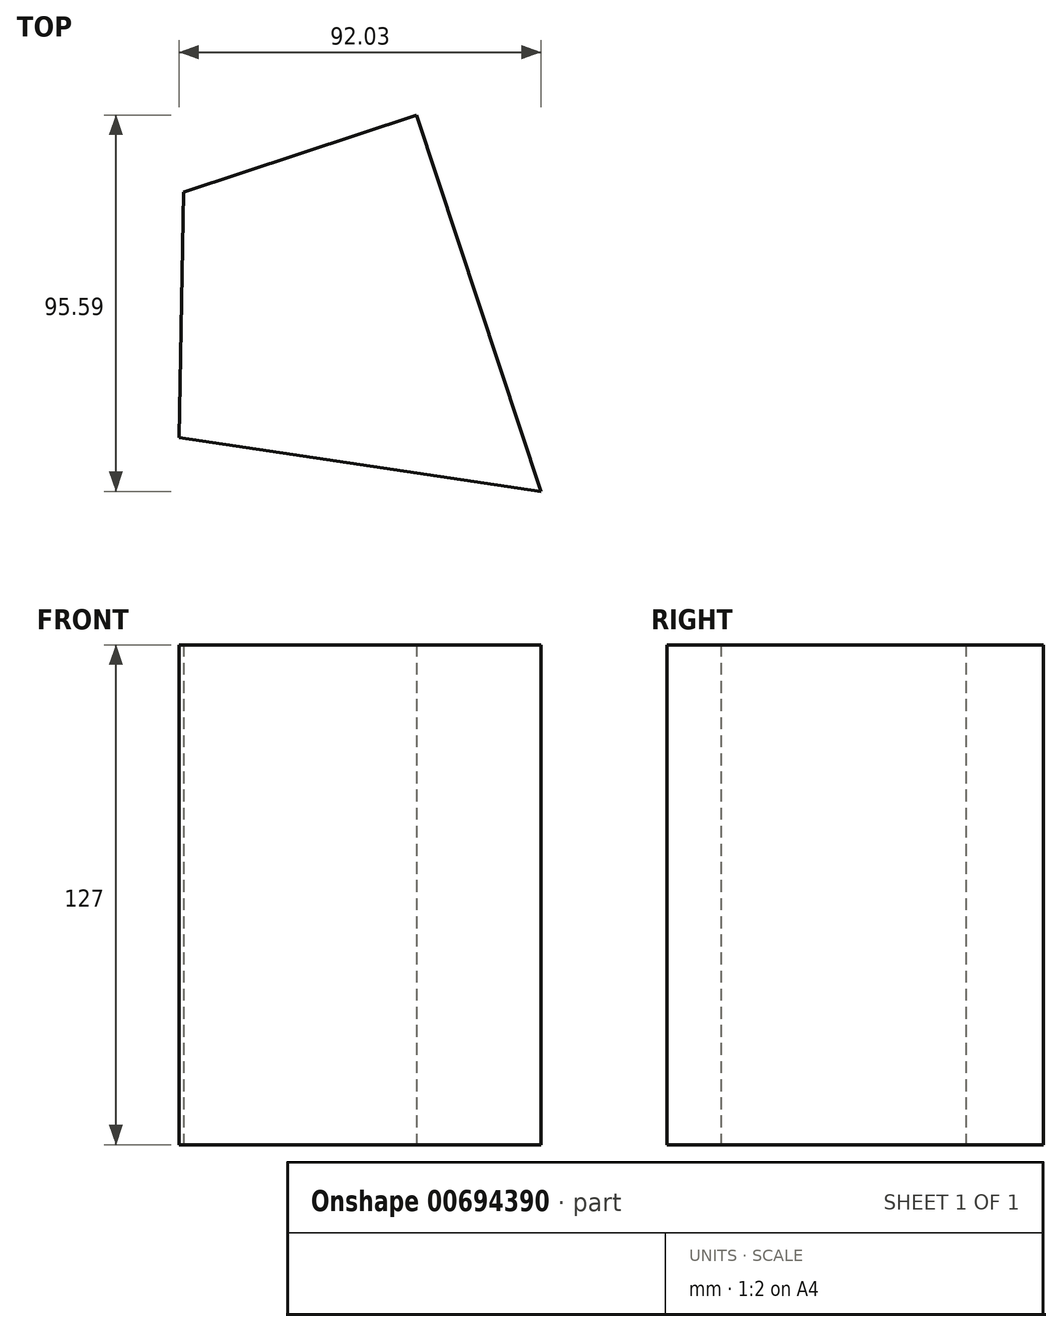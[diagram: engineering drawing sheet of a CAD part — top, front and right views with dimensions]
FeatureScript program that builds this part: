
annotation { "Feature Type Name" : "Feature", "Feature Type Description" : "" }
export const myFeature = defineFeature(function(context is Context, id is Id, definition is map)
    precondition{}
    {
        {
            var Q0;
            Q0=qCreatedBy(makeId("Top.planeOp"),FACE);
            var sketch = newSketch(context, id + "F0", { "sketchPlane" : qUnion([Q0])});
            skLineSegment(sketch, "E0", {"start": v(-38.65, 26.73) * mm, "end": v(20.57, 46.34) * mm});
            skLineSegment(sketch, "E1", {"start": v(20.57, 46.34) * mm, "end": v(52.23, -49.25) * mm});
            skLineSegment(sketch, "E2", {"start": v(52.23, -49.25) * mm, "end": v(-39.8, -35.57) * mm});
            skLineSegment(sketch, "E3", {"start": v(-39.8, -35.57) * mm, "end": v(-38.65, 26.73) * mm});
            skSolve(sketch);
        }
        {
            var Q0;
            Q0=makeQuery(id+"F0.imprint","IMPRINT",FACE,{"disambiguationData":[TD([[makeQuery(id+"F0.imprint","IMPRINT",EDGE,{"derivedFrom":sQuery(id+"F0.wireOp",EDGE,"E0")}),-1.0]])]});
            extrude(context, id + "F1", {"entities" : qUnion([Q0]), "depth" : 127 * mm, "offsetDistance" : 25.4 * mm});
        }
    });
